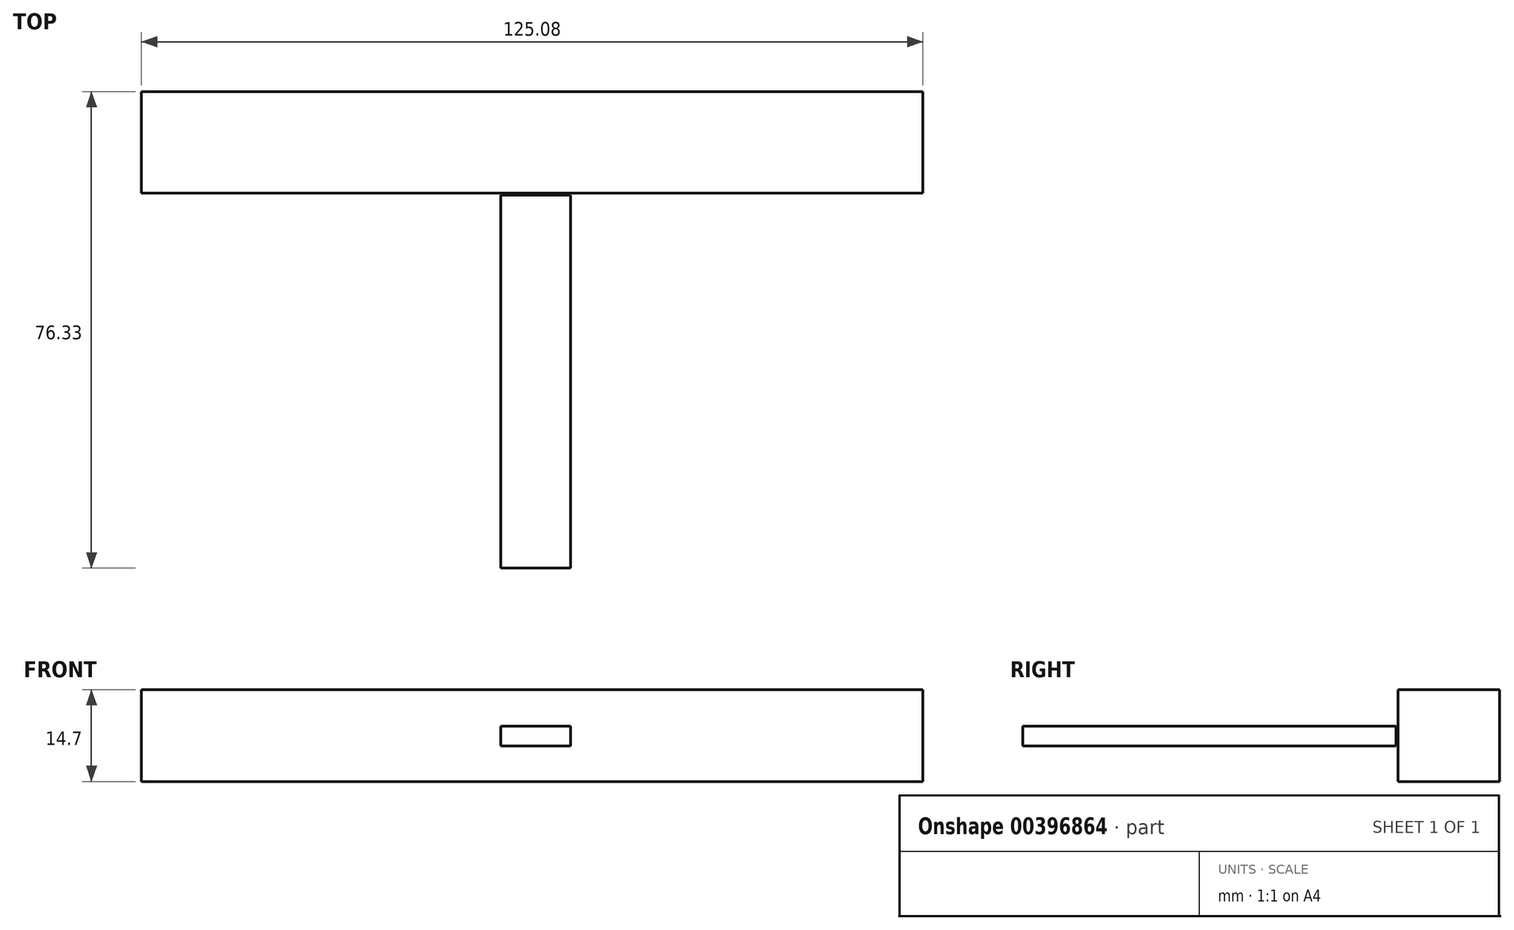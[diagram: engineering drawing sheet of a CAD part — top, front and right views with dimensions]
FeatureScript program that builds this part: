
annotation { "Feature Type Name" : "Feature", "Feature Type Description" : "" }
export const myFeature = defineFeature(function(context is Context, id is Id, definition is map)
    precondition{}
    {
        {
            var Q0;
            Q0=qCreatedBy(makeId("Front.planeOp"),FACE);
            var sketch = newSketch(context, id + "F0", { "sketchPlane" : qUnion([Q0])});
            skLineSegment(sketch, "E0.bottom", {"start": v(-57.48, 19.86) * mm, "end": v(67.6, 19.86) * mm});
            skLineSegment(sketch, "E0.top", {"start": v(-57.48, 5.16) * mm, "end": v(67.6, 5.16) * mm});
            skLineSegment(sketch, "E0.left", {"start": v(-57.48, 19.86) * mm, "end": v(-57.48, 5.16) * mm});
            skLineSegment(sketch, "E0.right", {"start": v(67.6, 19.86) * mm, "end": v(67.6, 5.16) * mm});
            skSolve(sketch);
        }
        {
            var Q0;
            Q0=makeQuery(id+"F0.imprint","IMPRINT",FACE,{"disambiguationData":[TD([[makeQuery(id+"F0.imprint","IMPRINT",EDGE,{"derivedFrom":sQuery(id+"F0.wireOp",EDGE,"E0.bottom")}),-1.0]])]});
            extrude(context, id + "F1", {"entities" : qUnion([Q0]), "depth" : 16.26 * mm});
        }
        {
            var Q0;
            Q0=qCreatedBy(makeId("Right.planeOp"),FACE);
            var sketch = newSketch(context, id + "F2", { "sketchPlane" : qUnion([Q0])});
            skLineSegment(sketch, "E1.bottom", {"start": v(-16.56, 14) * mm, "end": v(-76.33, 14) * mm});
            skLineSegment(sketch, "E1.top", {"start": v(-16.56, 10.83) * mm, "end": v(-76.33, 10.83) * mm});
            skLineSegment(sketch, "E1.left", {"start": v(-16.56, 14) * mm, "end": v(-16.56, 10.83) * mm});
            skLineSegment(sketch, "E1.right", {"start": v(-76.33, 14) * mm, "end": v(-76.33, 10.83) * mm});
            skSolve(sketch);
        }
        {
            var Q0;
            Q0=makeQuery(id+"F2.imprint","IMPRINT",FACE,{"disambiguationData":[TD([[makeQuery(id+"F2.imprint","IMPRINT",EDGE,{"derivedFrom":sQuery(id+"F2.wireOp",EDGE,"E1.bottom")}),1.0]])]});
            extrude(context, id + "F3", {"entities" : qUnion([Q0]), "depth" : 11.18 * mm});
        }
    });
